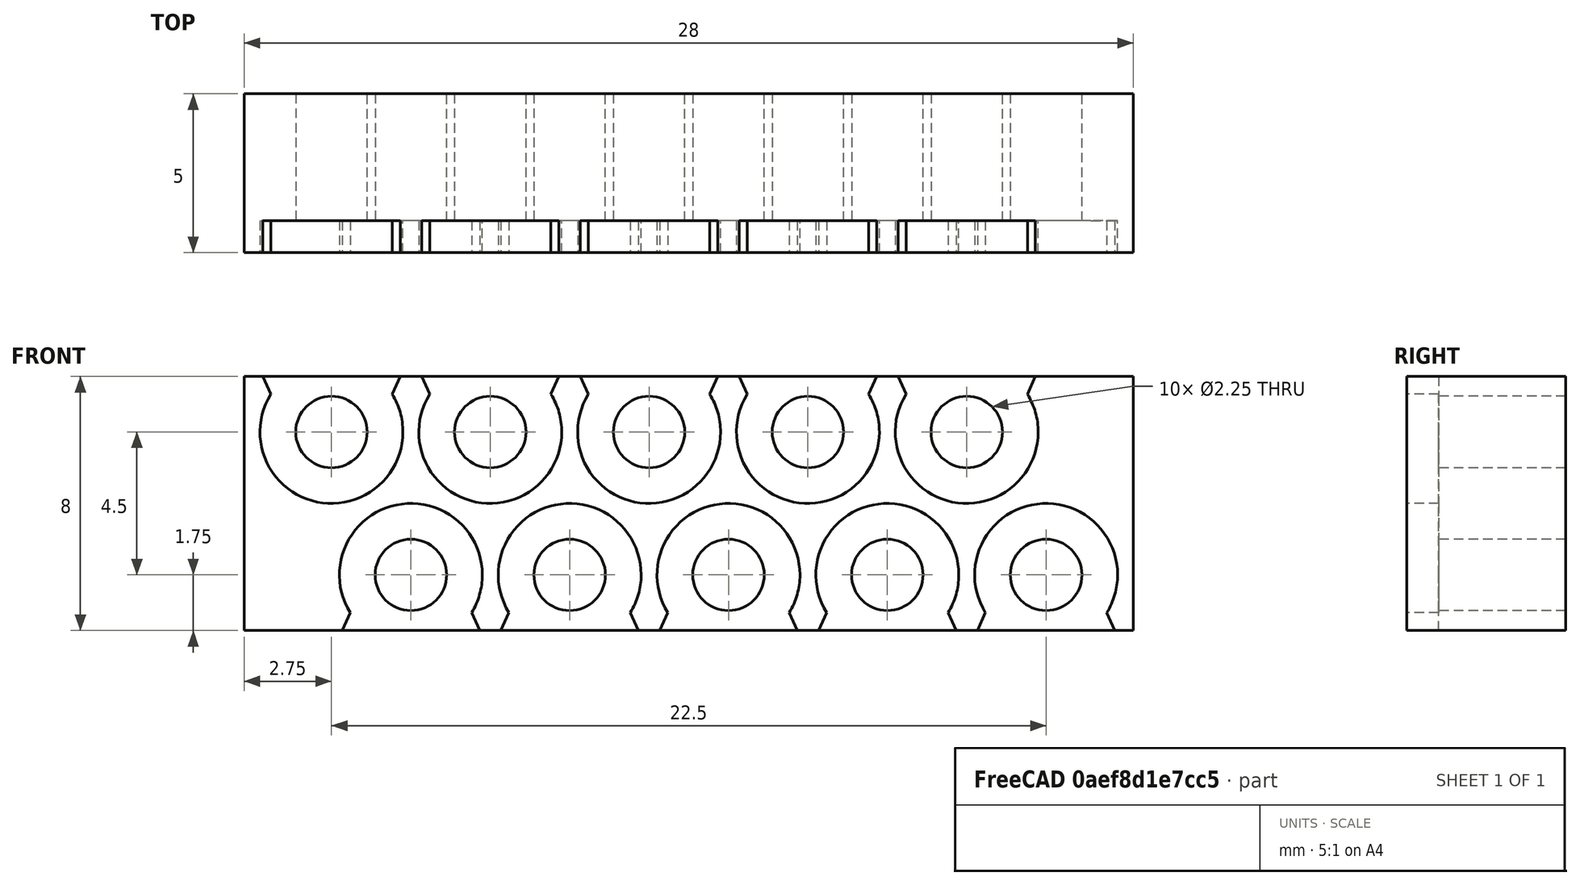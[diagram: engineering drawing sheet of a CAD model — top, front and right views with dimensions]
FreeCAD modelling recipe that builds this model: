
FCSTD DOCUMENT  (FreeCAD 0.19R)
Label: Junction10x
License: All rights reserved
LicenseURL: http://en.wikipedia.org/wiki/All_rights_reserved
objects: Sketcher::SketchObject×3, PartDesign::Pocket×2, PartDesign::Pad×1, PartDesign::Chamfer×1, PartDesign::Body×1, Mesh::Feature×1
note: 12 computed .brp shape members not serialized (recipe doc carries the construction recipe); baked Part::Feature solids carry a one-line shape summary decoded from their .brp

FEATURE [Sketcher::SketchObject] Sketch
  FullyConstrained = true
  MapMode = 5
  Placement = pos=(0,0,0) rot=(1,0,0;1.5708rad)
  Support = -> [XZ_Plane]
  sketch-geometry (4):
    g0: LineSegment StartX=-14 StartY=8 StartZ=0 EndX=14 EndY=8 EndZ=0
    g1: LineSegment StartX=14 StartY=8 StartZ=0 EndX=14 EndY=0 EndZ=0
    g2: LineSegment StartX=14 StartY=0 StartZ=0 EndX=-14 EndY=0 EndZ=0
    g3: LineSegment StartX=-14 StartY=0 StartZ=0 EndX=-14 EndY=8 EndZ=0
  constraints (11):
    c: Coincident(g0,g1)
    c: Coincident(g1,g2)
    c: Coincident(g2,g3)
    c: Coincident(g3,g0)
    c: Horizontal(g0)
    c: Horizontal(g2)
    c: Vertical(g1)
    c: Vertical(g3)
    c: Symmetric(g2,g1,g-1)
    c: Distance(g1) = 8
    c: Distance(g0) = 28
FEATURE [PartDesign::Pad] Pad
  Direction = (1,1,1)
  Length = 3
  Length2 = 2
  Placement = pos=(0,0,0) rot=(1,0,0;1.5708rad)
  Profile = -> Sketch
  Type = 4
FEATURE [Sketcher::SketchObject] Sketch001
  FullyConstrained = false
  MapMode = 5
  Placement = pos=(0,-3,2e-15) rot=(1,0,0;1.5708rad)
  Support = -> [Pad]
  sketch-geometry (23):
    g0: Circle CenterX=-11.25 CenterY=6.25 CenterZ=0 NormalX=0 NormalY=0 NormalZ=1 AngleXU=0 Radius=1.125
    g1: Circle CenterX=-8.75 CenterY=1.75 CenterZ=0 NormalX=0 NormalY=0 NormalZ=1 AngleXU=0 Radius=1.125
    g2: Circle CenterX=-6.25 CenterY=6.25 CenterZ=0 NormalX=0 NormalY=0 NormalZ=1 AngleXU=0 Radius=1.125
    g3: Circle CenterX=-3.75 CenterY=1.75 CenterZ=0 NormalX=0 NormalY=0 NormalZ=1 AngleXU=0 Radius=1.125
    g4: Circle CenterX=-1.25 CenterY=6.25 CenterZ=0 NormalX=0 NormalY=0 NormalZ=1 AngleXU=0 Radius=1.125
    g5: Circle CenterX=1.25 CenterY=1.75 CenterZ=0 NormalX=0 NormalY=0 NormalZ=1 AngleXU=0 Radius=1.125
    g6: Circle CenterX=3.75 CenterY=6.25 CenterZ=0 NormalX=0 NormalY=0 NormalZ=1 AngleXU=0 Radius=1.125
    g7: Circle CenterX=6.25 CenterY=1.75 CenterZ=0 NormalX=0 NormalY=0 NormalZ=1 AngleXU=0 Radius=1.125
    g8: Circle CenterX=8.75 CenterY=6.25 CenterZ=0 NormalX=0 NormalY=0 NormalZ=1 AngleXU=0 Radius=1.125
    g9: Circle CenterX=11.25 CenterY=1.75 CenterZ=0 NormalX=0 NormalY=0 NormalZ=1 AngleXU=0 Radius=1.125
    g10: LineSegment StartX=-13.279 StartY=1.75 StartZ=0 EndX=14.3254 EndY=1.75 EndZ=0
    g11: LineSegment StartX=-14.6773 StartY=6.25 StartZ=0 EndX=13.3509 EndY=6.25 EndZ=0
    g12: Circle CenterX=-11.25 CenterY=6.25 CenterZ=0 NormalX=0 NormalY=0 NormalZ=1 AngleXU=0 Radius=2.25
    g13: Circle CenterX=-6.25 CenterY=6.25 CenterZ=0 NormalX=0 NormalY=0 NormalZ=1 AngleXU=0 Radius=2.25
    g14: Circle CenterX=-1.25 CenterY=6.25 CenterZ=0 NormalX=0 NormalY=0 NormalZ=1 AngleXU=0 Radius=2.25
    g15: Circle CenterX=3.75 CenterY=6.25 CenterZ=0 NormalX=0 NormalY=0 NormalZ=1 AngleXU=0 Radius=2.25
    g16: Circle CenterX=8.75 CenterY=6.25 CenterZ=0 NormalX=0 NormalY=0 NormalZ=1 AngleXU=0 Radius=2.25
    g17: Circle CenterX=11.25 CenterY=1.75 CenterZ=0 NormalX=0 NormalY=0 NormalZ=1 AngleXU=0 Radius=2.25
    g18: Circle CenterX=6.25 CenterY=1.75 CenterZ=0 NormalX=0 NormalY=0 NormalZ=1 AngleXU=0 Radius=2.25
    g19: Circle CenterX=1.25 CenterY=1.75 CenterZ=0 NormalX=0 NormalY=0 NormalZ=1 AngleXU=0 Radius=2.25
    g20: Circle CenterX=-3.75 CenterY=1.75 CenterZ=0 NormalX=0 NormalY=0 NormalZ=1 AngleXU=0 Radius=2.25
    g21: Circle CenterX=-8.75 CenterY=1.75 CenterZ=0 NormalX=0 NormalY=0 NormalZ=1 AngleXU=0 Radius=2.25
    g22: Circle CenterX=11.25 CenterY=6.25 CenterZ=0 NormalX=0 NormalY=0 NormalZ=1 AngleXU=0 Radius=0.905036
  constraints (47):
    c: Diameter(g0) = 2.25
    c: Equal(g0, g1-g9) x9
    c: Horizontal(g10)
    c: Horizontal(g11)
    c: PointOnObject(g0,g11)
    c: PointOnObject(g2,g11)
    c: PointOnObject(g4,g11)
    c: PointOnObject(g6,g11)
    c: PointOnObject(g8,g11)
    c: PointOnObject(g7,g10)
    c: PointOnObject(g9,g10)
    c: PointOnObject(g5,g10)
    c: PointOnObject(g3,g10)
    c: PointOnObject(g1,g10)
    c: Coincident(g12,g0)
    c: Coincident(g13,g2)
    c: Coincident(g14,g4)
    c: Coincident(g15,g6)
    c: Coincident(g16,g8)
    c: Coincident(g17,g9)
    c: Coincident(g18,g7)
    c: Coincident(g19,g5)
    c: Coincident(g20,g3)
    c: Coincident(g21,g1)
    c: Diameter(g12) = 4.5
    c: Equal(g12,g21)
    c: Equal(g12,g13)
    c: Equal(g12,g20)
    c: Equal(g12,g14)
    c: Equal(g12,g15)
    c: Equal(g12,g19)
    c: Equal(g12,g16)
    c: Equal(g12,g18)
    c: Equal(g12,g17)
    c: Distance(g0,g2) = 5
    c: Distance(g4,g2) = 5
    c: Distance(g6,g4) = 5
    c: Distance(g6,g8) = 5
    c: Distance(g1,g3) = 5
    c: Distance(g3,g5) = 5
    c: Distance(g5,g7) = 5
    c: Distance(g9,g7) = 5
    c: DistanceX(g0,g1) = 2.5
    c: Distance(g10,g11) = 4.5
    c: DistanceY(g10) = 1.75
    c: Distance(g22,g8) = 2.5
    c: Symmetric(g0,g22,g-2)
FEATURE [PartDesign::Pocket] Pocket
  BaseFeature = -> Pad
  Length = 5
  Length2 = 100
  Placement = pos=(0,0,0) rot=(1,0,0;1.5708rad)
  Profile = -> Sketch001
  Type = 0
FEATURE [Sketcher::SketchObject] Sketch003
  FullyConstrained = false
  MapMode = 5
  Placement = pos=(0,-3,3.3e-15) rot=(1,0,0;1.5708rad)
  Support = -> [Pocket]
  sketch-geometry (23):
    g0: Circle CenterX=-11.25 CenterY=6.25 CenterZ=0 NormalX=0 NormalY=0 NormalZ=1 AngleXU=0 Radius=1.125
    g1: Circle CenterX=-8.75 CenterY=1.75 CenterZ=0 NormalX=0 NormalY=0 NormalZ=1 AngleXU=0 Radius=1.125
    g2: Circle CenterX=-6.25 CenterY=6.25 CenterZ=0 NormalX=0 NormalY=0 NormalZ=1 AngleXU=0 Radius=1.125
    g3: Circle CenterX=-3.75 CenterY=1.75 CenterZ=0 NormalX=0 NormalY=0 NormalZ=1 AngleXU=0 Radius=1.125
    g4: Circle CenterX=-1.25 CenterY=6.25 CenterZ=0 NormalX=0 NormalY=0 NormalZ=1 AngleXU=0 Radius=1.125
    g5: Circle CenterX=1.25 CenterY=1.75 CenterZ=0 NormalX=0 NormalY=0 NormalZ=1 AngleXU=0 Radius=1.125
    g6: Circle CenterX=3.75 CenterY=6.25 CenterZ=0 NormalX=0 NormalY=0 NormalZ=1 AngleXU=0 Radius=1.125
    g7: Circle CenterX=6.25 CenterY=1.75 CenterZ=0 NormalX=0 NormalY=0 NormalZ=1 AngleXU=0 Radius=1.125
    g8: Circle CenterX=8.75 CenterY=6.25 CenterZ=0 NormalX=0 NormalY=0 NormalZ=1 AngleXU=0 Radius=1.125
    g9: Circle CenterX=11.25 CenterY=1.75 CenterZ=0 NormalX=0 NormalY=0 NormalZ=1 AngleXU=0 Radius=1.125
    g10: LineSegment StartX=-13.279 StartY=1.75 StartZ=0 EndX=14.3254 EndY=1.75 EndZ=0
    g11: LineSegment StartX=-14.6773 StartY=6.25 StartZ=0 EndX=13.3509 EndY=6.25 EndZ=0
    g12: Circle CenterX=-11.25 CenterY=6.25 CenterZ=0 NormalX=0 NormalY=0 NormalZ=1 AngleXU=0 Radius=2.25
    g13: Circle CenterX=-6.25 CenterY=6.25 CenterZ=0 NormalX=0 NormalY=0 NormalZ=1 AngleXU=0 Radius=2.25
    g14: Circle CenterX=-1.25 CenterY=6.25 CenterZ=0 NormalX=0 NormalY=0 NormalZ=1 AngleXU=0 Radius=2.25
    g15: Circle CenterX=3.75 CenterY=6.25 CenterZ=0 NormalX=0 NormalY=0 NormalZ=1 AngleXU=0 Radius=2.25
    g16: Circle CenterX=8.75 CenterY=6.25 CenterZ=0 NormalX=0 NormalY=0 NormalZ=1 AngleXU=0 Radius=2.25
    g17: Circle CenterX=11.25 CenterY=1.75 CenterZ=0 NormalX=0 NormalY=0 NormalZ=1 AngleXU=0 Radius=2.25
    g18: Circle CenterX=6.25 CenterY=1.75 CenterZ=0 NormalX=0 NormalY=0 NormalZ=1 AngleXU=0 Radius=2.25
    g19: Circle CenterX=1.25 CenterY=1.75 CenterZ=0 NormalX=0 NormalY=0 NormalZ=1 AngleXU=0 Radius=2.25
    g20: Circle CenterX=-3.75 CenterY=1.75 CenterZ=0 NormalX=0 NormalY=0 NormalZ=1 AngleXU=0 Radius=2.25
    g21: Circle CenterX=-8.75 CenterY=1.75 CenterZ=0 NormalX=0 NormalY=0 NormalZ=1 AngleXU=0 Radius=2.25
    g22: Circle CenterX=11.25 CenterY=6.25 CenterZ=0 NormalX=0 NormalY=0 NormalZ=1 AngleXU=0 Radius=0.905036
  constraints (47):
    c: Diameter(g0) = 2.25
    c: Equal(g0, g1-g9) x9
    c: Horizontal(g10)
    c: Horizontal(g11)
    c: PointOnObject(g0,g11)
    c: PointOnObject(g2,g11)
    c: PointOnObject(g4,g11)
    c: PointOnObject(g6,g11)
    c: PointOnObject(g8,g11)
    c: PointOnObject(g7,g10)
    c: PointOnObject(g9,g10)
    c: PointOnObject(g5,g10)
    c: PointOnObject(g3,g10)
    c: PointOnObject(g1,g10)
    c: Coincident(g12,g0)
    c: Coincident(g13,g2)
    c: Coincident(g14,g4)
    c: Coincident(g15,g6)
    c: Coincident(g16,g8)
    c: Coincident(g17,g9)
    c: Coincident(g18,g7)
    c: Coincident(g19,g5)
    c: Coincident(g20,g3)
    c: Coincident(g21,g1)
    c: Diameter(g12) = 4.5
    c: Equal(g12,g21)
    c: Equal(g12,g13)
    c: Equal(g12,g20)
    c: Equal(g12,g14)
    c: Equal(g12,g15)
    c: Equal(g12,g19)
    c: Equal(g12,g16)
    c: Equal(g12,g18)
    c: Equal(g12,g17)
    c: Distance(g0,g2) = 5
    c: Distance(g4,g2) = 5
    c: Distance(g6,g4) = 5
    c: Distance(g6,g8) = 5
    c: Distance(g1,g3) = 5
    c: Distance(g3,g5) = 5
    c: Distance(g5,g7) = 5
    c: Distance(g9,g7) = 5
    c: DistanceX(g0,g1) = 2.5
    c: Distance(g10,g11) = 4.5
    c: DistanceY(g10) = 1.75
    c: Distance(g22,g8) = 2.5
    c: Symmetric(g0,g22,g-2)
FEATURE [PartDesign::Pocket] Pocket001
  BaseFeature = -> Pocket
  Length = 1
  Length2 = 100
  Placement = pos=(0,0,0) rot=(1,0,0;1.5708rad)
  Profile = -> Sketch003
  Type = 0
FEATURE [PartDesign::Chamfer] Chamfer
  Angle = 45
  Base = -> Pocket001 [Edge88,Edge90,Edge91,Edge93,Edge94,Edge96,Edge97,Edge99,Edge100,Edge102,Edge4,Edge6,Edge8,Edge10,Edge12,Edge14,Edge16,Edge18,Edge20,Edge22]
  BaseFeature = -> Pocket001
  ChamferType = 0
  FlipDirection = false
  Placement = pos=(0,0,0) rot=(1,0,0;1.5708rad)
  Size = 0.75
  Size2 = 1
  SupportTransform = false
FEATURE [PartDesign::Body] Body
  Group = -> [Sketch,Pad,Sketch001,Pocket,Sketch003,Pocket001,Chamfer]
  Origin = -> Origin
  Tip = -> Chamfer
FEATURE [Mesh::Feature] Mesh  label="Chamfer (Meshed)"
